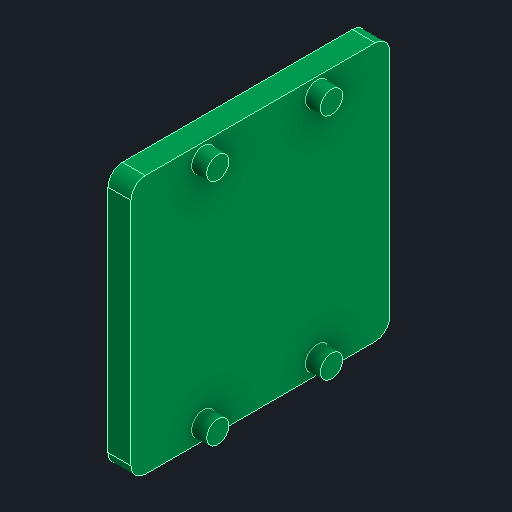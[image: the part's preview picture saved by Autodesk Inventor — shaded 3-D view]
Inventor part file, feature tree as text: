
AUTODESK INVENTOR PART (.ipt)
format: ipt  version: 2023.4 (Build 274418000, 418)  size: 127,488 bytes
history: native  units: mm
features: chamfer x4, plane x3, other x3, sketch x2, extrude x2, reference x2
ambient origin geometry x8: Origin, YZ Plane, XZ Plane, XY Plane, X Axis, Y Axis, Z Axis, Center Point
bodies: Solid1 (feature_tree)
feature tree (16):
  plane  "Work Plane1"
  sketch  "Sketch1"  dims[d0=10.0mm d1=0.0mm d2=10.0mm d3=0.0mm]
  plane  "Work Plane2"
  extrude  "Extrusion1"  Depth=10.0mm TaperAngle=0.0deg
  sketch  "Sketch2"  dims[d4=0.125mm d5=2.5mm d6=45.0deg d7=0.125mm d8=2.5mm d9=45.0deg d10=0.125mm d11=2.5mm d12=45.0deg d13=0.125mm d14=2.5mm d15=45.0deg]
  plane  "Work Plane3"
  extrude  "Extrusion2"  Depth=2.5mm TaperAngle=45.0deg
  chamfer  "Chamfer1"  Distance=2.5mm Angle=45.0deg
  chamfer  "Chamfer2"  Distance=2.5mm Angle=45.0deg
  chamfer  "Chamfer3"  [1 undecoded]
  chamfer  "Chamfer4"  [1 undecoded]
  reference  "Reference1"
  reference  "Reference2"
  other  "<path>\Projects\Project Protocube\Protocube\CAD, STL, OBJ Files\1 CAD\Cube 1x1 V5.iam"
  other  "Cube 1x1 V5.iam"
  other  "Outer Cover Side Open:1"
note: 2 required parameter values undecoded (feature->parameter linkage not recoverable at this tier; creation-order binding heuristic only, values carry confidence <= 0.55)
note: 1 file-system path scrubbed to <path> (originals preserved in map.json)
